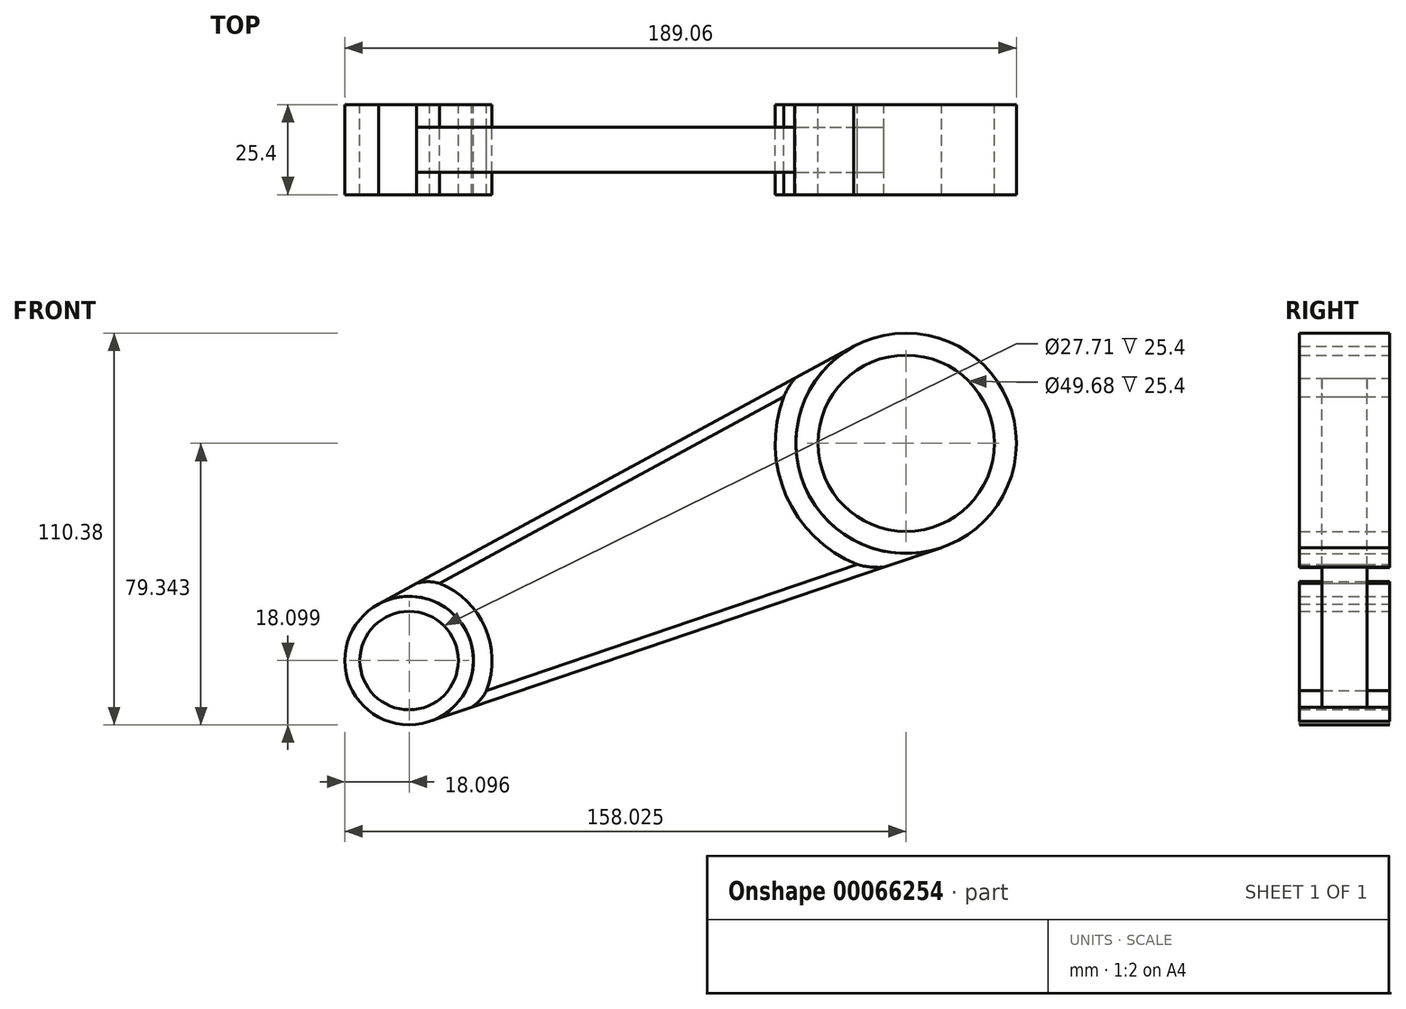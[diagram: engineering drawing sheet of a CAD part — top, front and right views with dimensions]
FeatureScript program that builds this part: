
annotation { "Feature Type Name" : "Feature", "Feature Type Description" : "" }
export const myFeature = defineFeature(function(context is Context, id is Id, definition is map)
    precondition{}
    {
        {
            var Q0;
            Q0=qCreatedBy(makeId("Front.planeOp"),FACE);
            var sketch = newSketch(context, id + "F0", { "sketchPlane" : qUnion([Q0])});
            skLineSegment(sketch, "E0.bottom", {"start": v(-67.75, 57.45) * mm, "end": v(60.14, 57.45) * mm});
            skLineSegment(sketch, "E0.top", {"start": v(-67.75, -47.02) * mm, "end": v(60.14, -47.02) * mm});
            skLineSegment(sketch, "E0.left", {"start": v(-67.75, 57.45) * mm, "end": v(-67.75, -47.02) * mm});
            skLineSegment(sketch, "E0.right", {"start": v(60.14, 57.45) * mm, "end": v(60.14, -47.02) * mm});
            skCircle(sketch, "E1", {"center": v(-67.75, 57.45) * mm, "radius": 19.9 * mm});
            skCircle(sketch, "E2", {"center": v(60.14, 57.45) * mm, "radius": 19.9 * mm});
            skCircle(sketch, "E3", {"center": v(-67.75, -47.02) * mm, "radius": 19.9 * mm});
            skCircle(sketch, "E4", {"center": v(60.14, -47.02) * mm, "radius": 19.9 * mm});
            skCircle(sketch, "E5", {"center": v(-3.8, 57.45) * mm, "radius": 12.68 * mm});
            skCircle(sketch, "E6", {"center": v(-67.75, 5.22) * mm, "radius": 12.68 * mm});
            skCircle(sketch, "E7", {"center": v(-3.8, -47.02) * mm, "radius": 12.68 * mm});
            skCircle(sketch, "E8", {"center": v(60.14, 5.22) * mm, "radius": 12.68 * mm});
            skSolve(sketch);
        }
        {
            var Q0;
            Q0=qCreatedBy(makeId("Front.planeOp"),FACE);
            var sketch = newSketch(context, id + "F1", { "sketchPlane" : qUnion([Q0])});
            skLineSegment(sketch, "E9.bottom", {"start": v(0, 0) * mm, "end": v(0, 0) * mm});
            skLineSegment(sketch, "E9.top", {"start": v(0, 0) * mm, "end": v(0, 0) * mm});
            skLineSegment(sketch, "E9.left", {"start": v(0, 0) * mm, "end": v(0, 0) * mm});
            skLineSegment(sketch, "E9.right", {"start": v(0, 0) * mm, "end": v(0, 0) * mm});
            skLineSegment(sketch, "E10.bottom", {"start": v(-38.19, 52.83) * mm, "end": v(71.97, 52.83) * mm});
            skLineSegment(sketch, "E10.top", {"start": v(-38.19, -57.33) * mm, "end": v(71.97, -57.33) * mm});
            skLineSegment(sketch, "E10.left", {"start": v(-38.19, 52.83) * mm, "end": v(-38.19, -57.33) * mm});
            skLineSegment(sketch, "E10.right", {"start": v(71.97, 52.83) * mm, "end": v(71.97, -57.33) * mm});
            skArc(sketch, "E11", {"start": v(16.9, 52.83) * mm, "mid": v(-10.65, 80.37) * mm, "end": v(-38.19, 52.83) * mm});
            skArc(sketch, "E12", {"start": v(71.97, 52.83) * mm, "mid": v(44.43, 80.37) * mm, "end": v(16.9, 52.83) * mm});
            skArc(sketch, "E13", {"start": v(71.97, -2.25) * mm, "mid": v(99.51, 25.29) * mm, "end": v(71.97, 52.83) * mm});
            skArc(sketch, "E14", {"start": v(71.97, -57.33) * mm, "mid": v(99.51, -29.8) * mm, "end": v(71.97, -2.25) * mm});
            skArc(sketch, "E15", {"start": v(16.9, -57.33) * mm, "mid": v(44.43, -84.87) * mm, "end": v(71.97, -57.33) * mm});
            skArc(sketch, "E16", {"start": v(-38.19, -57.33) * mm, "mid": v(-10.65, -84.87) * mm, "end": v(16.9, -57.33) * mm});
            skSolve(sketch);
        }
        {
            var Q0;
            Q0=qCreatedBy(makeId("Front.planeOp"),FACE);
            var sketch = newSketch(context, id + "F2", { "sketchPlane" : qUnion([Q0])});
            skCircle(sketch, "E17", {"center": v(-126.17, 3.79) * mm, "radius": 18.1 * mm});
            skCircle(sketch, "E18", {"center": v(13.76, 65.03) * mm, "radius": 31.03 * mm});
            skLineSegment(sketch, "E19", {"start": v(-120.35, -13.34) * mm, "end": v(23.75, 35.65) * mm});
            skLineSegment(sketch, "E20", {"start": v(-134.8, 19.7) * mm, "end": v(-1.05, 92.3) * mm});
            skCircle(sketch, "E21", {"center": v(-126.17, 3.79) * mm, "radius": 13.85 * mm});
            skCircle(sketch, "E22", {"center": v(13.76, 65.03) * mm, "radius": 24.84 * mm});
            skArc(sketch, "E23", {"start": v(-104.4, -4.66) * mm, "mid": v(-104.77, 13.16) * mm, "end": v(-117.6, 25.52) * mm});
            skArc(sketch, "E24", {"start": v(-20.7, 78.13) * mm, "mid": v(-20.01, 50.25) * mm, "end": v(0, 30.83) * mm});
            skLineSegment(sketch, "E25", {"start": v(-117.6, 25.52) * mm, "end": v(-20.7, 78.13) * mm});
            skLineSegment(sketch, "E26", {"start": v(-104.4, -4.66) * mm, "end": v(0, 30.83) * mm});
            skArc(sketch, "E27", {"start": v(0, 30.83) * mm, "mid": v(3.69, 30.17) * mm, "end": v(7.43, 30.1) * mm});
            skArc(sketch, "E28", {"start": v(-17.6, 83.32) * mm, "mid": v(-19.32, 80.83) * mm, "end": v(-20.7, 78.13) * mm});
            skArc(sketch, "E29", {"start": v(-117.6, 25.52) * mm, "mid": v(-120.84, 26) * mm, "end": v(-124.07, 25.52) * mm});
            skArc(sketch, "E30", {"start": v(-108.59, -9.34) * mm, "mid": v(-106.15, -7.3) * mm, "end": v(-104.4, -4.66) * mm});
            skSolve(sketch);
        }
        {
            var Q0;
            Q0=makeQuery(id+"F2.imprint","IMPRINT",FACE,{"disambiguationData":[TD([[makeQuery(id+"F2.imprint","IMPRINT",EDGE,{"derivedFrom":sQuery(id+"F2.wireOp",EDGE,"E22")}),-1.0]])]});
            var Q1;
            Q1=makeQuery(id+"F2.imprint","IMPRINT",FACE,{"disambiguationData":[TD([[makeQuery(id+"F2.imprint","IMPRINT",EDGE,{"derivedFrom":sQuery(id+"F2.wireOp",EDGE,"E21")}),-1.0]])]});
            extrude(context, id + "F3", {"entities" : qUnion([Q0, Q1]), "endBound" : BoundingType.SYMMETRIC, "depth" : 25.4 * mm});
        }
        {
            var Q0;
            Q0=makeQuery(id+"F2.imprint","IMPRINT",FACE,{"disambiguationData":[TD([[makeQuery(id+"F2.imprint","IMPRINT",EDGE,{"derivedFrom":sQuery(id+"F2.wireOp",EDGE,"E24")}),1.0]])]});
            var Q1;
            Q1=makeQuery(id+"F2.imprint","IMPRINT",FACE,{"disambiguationData":[TD([[makeQuery(id+"F2.imprint","IMPRINT",EDGE,{"derivedFrom":sQuery(id+"F2.wireOp",EDGE,"E23")}),1.0]])]});
            extrude(context, id + "F4", {"entities" : qUnion([Q0, Q1]), "endBound" : BoundingType.SYMMETRIC, "depth" : 25.4 * mm});
        }
        {
            var Q0;
            Q0=makeQuery(id+"F2.imprint","IMPRINT",FACE,{"disambiguationData":[TD([[makeQuery(id+"F2.imprint","IMPRINT",EDGE,{"derivedFrom":sQuery(id+"F2.wireOp",EDGE,"E26")}),-1.0]])]});
            var Q1;
            Q1=makeQuery(id+"F2.imprint","IMPRINT",FACE,{"disambiguationData":[TD([[makeQuery(id+"F2.imprint","IMPRINT",EDGE,{"derivedFrom":sQuery(id+"F2.wireOp",EDGE,"E25")}),1.0]])]});
            extrude(context, id + "F5", {"entities" : qUnion([Q0, Q1]), "endBound" : BoundingType.SYMMETRIC, "depth" : 12.7 * mm});
        }
    });
